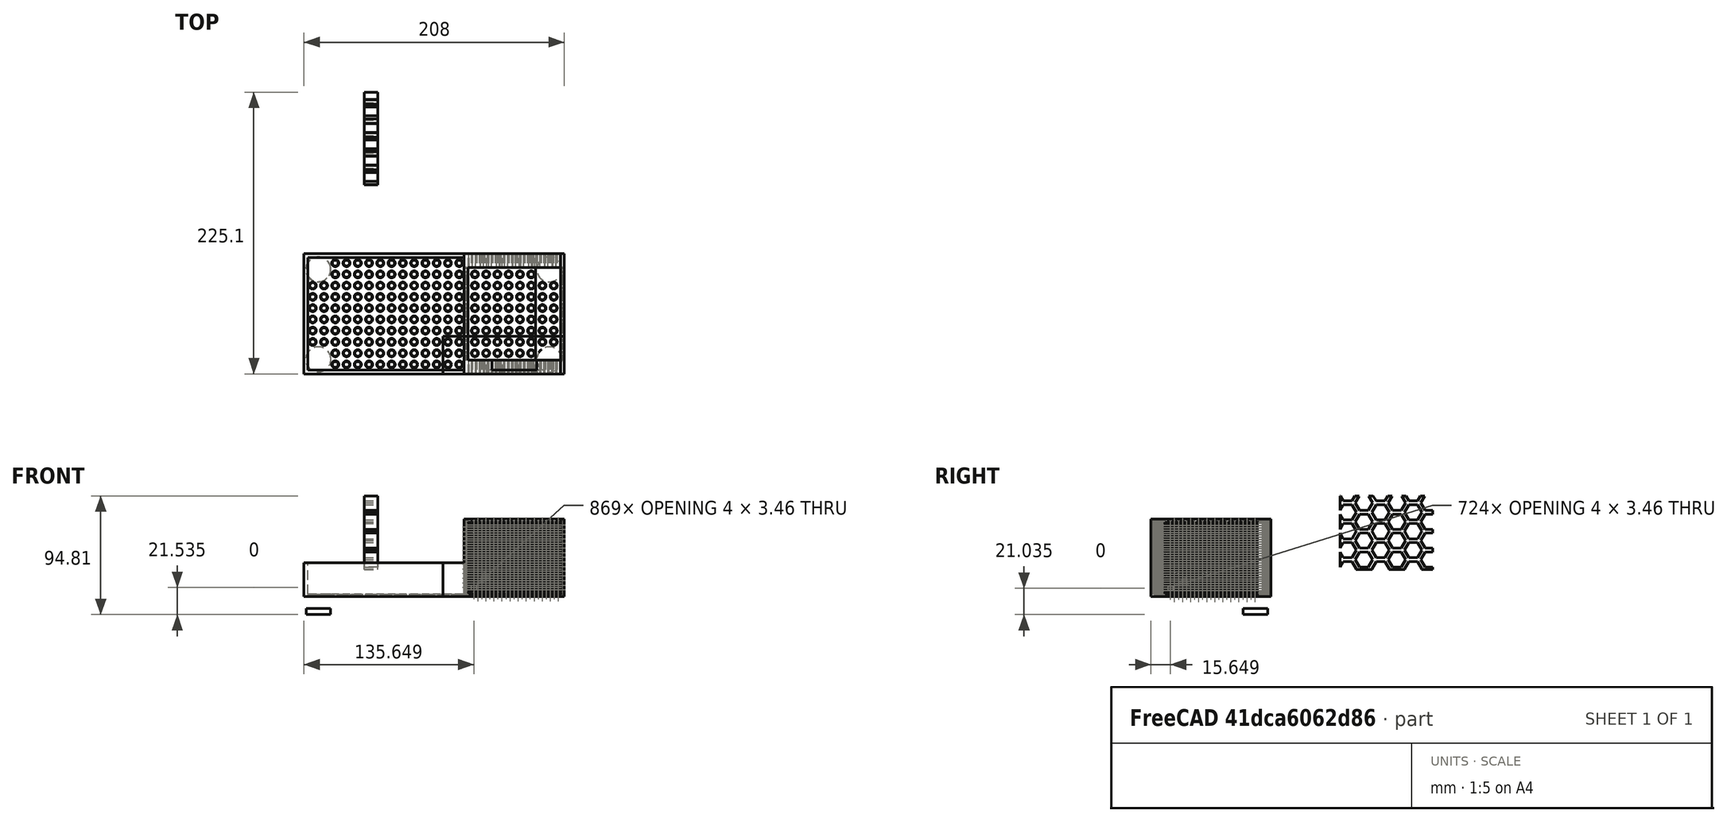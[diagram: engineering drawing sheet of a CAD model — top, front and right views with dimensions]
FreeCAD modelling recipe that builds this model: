
FCSTD DOCUMENT  (FreeCAD 0.19R24276 (Git))
Label: esponja_jabon19
License: All rights reserved
LicenseURL: http://en.wikipedia.org/wiki/All_rights_reserved
objects: Part::Box×18, Part::Cut×18, Part::Feature×10, Part::Cylinder×9, Part::MultiFuse×6, Part::FeaturePython×4, Mesh::Feature×3, Part::Cone×2, Spreadsheet::Sheet×1, Part::RegularPolygon×1, Part::Extrusion×1
note: 69 computed .brp shape members not serialized (recipe doc carries the construction recipe); baked Part::Feature solids carry a one-line shape summary decoded from their .brp

FEATURE [Part::Box] Box  label="Cube"
  AttacherType = Attacher::AttachEngine3D
  Height = 27
  Length = 128
  Width = 96
FEATURE [Part::Box] Box001  label="Cube001"
  AttacherType = Attacher::AttachEngine3D
  Height = 62
  Length = 125
  Placement = pos=(3,3,2) rot=(0,0,1;0rad)
  Width = 90
FEATURE [Part::Cut] Cut
  Base = -> Box
  Refine = true
  Tool = -> Box001
FEATURE [Part::Box] Box002  label="Cube002"
  AttacherType = Attacher::AttachEngine3D
  Height = 62
  Length = 80
  Placement = pos=(128,0,0) rot=(0,0,1;0rad)
  Width = 96
FEATURE [Part::Box] Box003  label="Cube003"
  AttacherType = Attacher::AttachEngine3D
  Height = 60
  Length = 74
  Placement = pos=(131,11,2) rot=(0,0,1;0rad)
  Width = 74
FEATURE [Part::Cone] Cone007  label="Cone001"
  Angle = 360
  AttacherType = Attacher::AttachEngine3D
  Height = 3
  Placement = pos=(7,7,0) rot=(0,0,1;0rad)
  Radius1 = 3
  Radius2 = 2.17
FEATURE [Part::Cone] Cone008
  Angle = 360
  AttacherType = Attacher::AttachEngine3D
  Height = 3
  Placement = pos=(135,16,0) rot=(0,0,1;0rad)
  Radius1 = 3
  Radius2 = 2.17
FEATURE [Part::Cylinder] Cylinder  label="Cylinder_up_left_add"
  Angle = 360
  AttacherType = Attacher::AttachEngine3D
  Height = 2
  Placement = pos=(11.5,11.5,0) rot=(0,0,1;0rad)
  Radius = 10
FEATURE [Part::Cylinder] Cylinder001  label="Cylinder001_down_left_add"
  Angle = 360
  AttacherType = Attacher::AttachEngine3D
  Height = 2
  Placement = pos=(11.5,83.5,0) rot=(0,0,1;0rad)
  Radius = 10
FEATURE [Part::Cylinder] Cylinder002  label="Cylinder002_up_right_Add"
  Angle = 360
  AttacherType = Attacher::AttachEngine3D
  Height = 2
  Placement = pos=(196,11.5,0) rot=(0,0,1;0rad)
  Radius = 10
FEATURE [Part::Cylinder] Cylinder003  label="Cylinder003_down_right_add"
  Angle = 360
  AttacherType = Attacher::AttachEngine3D
  Height = 2
  Placement = pos=(196,83.5,0) rot=(0,0,1;0rad)
  Radius = 10
FEATURE [Part::Cylinder] Cylinder004  label="Cylinder_up_left001_minus"
  Angle = 360
  AttacherType = Attacher::AttachEngine3D
  Height = 2
  Placement = pos=(11.5,11.5,-1.25) rot=(0,0,1;0rad)
  Radius = 10
FEATURE [Part::Cylinder] Cylinder005  label="Cylinder001_down_left001_minus"
  Angle = 360
  AttacherType = Attacher::AttachEngine3D
  Height = 2
  Placement = pos=(11.5,83.5,-1.25) rot=(0,0,1;0rad)
  Radius = 10
FEATURE [Part::Cylinder] Cylinder006  label="Cylinder002_up_right001_minus"
  Angle = 360
  AttacherType = Attacher::AttachEngine3D
  Height = 2
  Placement = pos=(196,11.5,-1.25) rot=(0,0,1;0rad)
  Radius = 10
FEATURE [Part::Cylinder] Cylinder007  label="Cylinder003_down_right001_minus"
  Angle = 360
  AttacherType = Attacher::AttachEngine3D
  Height = 2
  Placement = pos=(196,83.5,-1.25) rot=(0,0,1;0rad)
  Radius = 10
FEATURE [Spreadsheet::Sheet] EditMe
  cells = A1=User Variables; D1=Calculated Values; A2=Hexagon Radius:; B2(radius)=7; D2=X Interval:; E2(xInterval)==2 * sin(60deg) * (B2 * 2 + B3 - 0.267949 * B2); A3=Hexagon Separation:; B3(separation)=3; D3=Y Interval:; E3(yInterval)==2 * B2 + B3 - 0.267949 * B2; A4=Grid Width:; B4(width)=59; D4=First X:; E4(firstX)==B2; A5=Grid Length:; B5(length)=74; D5=First Y:; E5(firstY)==B2; A6=Grid Height:; B6(height)=11; D6=Count X:; E6(countX)==round(B5 / E2) + 2; D7=Count Y:; E7(countY)==round(B4 / E3) + 2; A8=Tweak X:; B8(tweakX)=0; D8=Array2 XPos:; E8(array2XPos)==sin(60deg) * (B2 * 2 + B3 - 0.267949 * B2); A9=Tweak Y:; B9(tweakY)=0; D9=Array2 YPos:; E9(array2YPos)==E3 / 2; A10=Tweak Z:; B10(tweakZ)=0; A11=Instructions:\n\nYou should only run the macro once unless you want to start again from scratch.\n\nEdit the values in column B to define your honeycomb.  You can also edit the objects (plate, arrays, etc.), but it's \nprobably better to do all the editing here in the spreadsheet at least until you get it more or less like you want it before\ndoing some final tweaking directly on the objects.\n\nHexagon radius -- the circumradius of the individual hexagons (circle with each vertex on its circumference).\n\nHexagon separation -- distance between each hexagon, the thickness of the grid produced after cutting the hexagons from the plate.\n\nPlate dimensions -- sets the dimensions of the plate out of which the honeycomb can be cut.  These values are used to calculate\nthe countX and countY variables.  You can delete the plate object if you wish to apply the hexagon arrays to a different structure.\n\nTweak X,Y,Z -- Edit these to move both hexagon arrays independently of the plate object, for example to center the arrays inside \nthe plate.\n\nCountX and CountY -- number of hexagons in the 2 arrays.  These are calculated based on the plate size, radius of hexagons, and \nseparation between them, but you will probably want to modify these manually.  Just remember if you modify them you are replacing \nthe formulas in those cells with immediate values, and thus they won't be recalulated for you if other changes are made.\n\nIf you would prefer a round plate, simply delete the plate object and replace it with a cylinder, and then use the Tweak values \nand countX and countY variables to arrange the hexagon arrays to your liking.
FEATURE [Part::RegularPolygon] HoneycombHexagon
  AttacherType = Attacher::AttachEngine3D
  Circumradius = 7
  Polygon = 6
  expr: Circumradius = EditMe.radius
FEATURE [Part::Extrusion] ExtrudedHexagon
  Base = -> HoneycombHexagon
  Dir = (0,0,1)
  DirMode = 0
  FaceMakerClass = Part::FaceMakerBullseye
  LengthFwd = 11
  LengthRev = 0
  Placement = pos=(7,7,0) rot=(0,0,1;0rad)
  Solid = true
  Symmetric = false
  expr: .Placement.Base.z = EditMe.tweakZ
  expr: .Placement.Base.y = EditMe.firstY + EditMe.tweakY
  expr: .Placement.Base.x = EditMe.firstX + EditMe.tweakX
  expr: LengthFwd = EditMe.height
FEATURE [Part::FeaturePython] HoneycombArray1  # Draft array (typed FeaturePython)
  Angle = 360
  ArrayType = 0
  Axis = (0,0,1)
  Base = -> ExtrudedHexagon
  Center = (0,0,0)
  Fuse = false
  IntervalAxis = (0,0,0)
  IntervalX = (26.1962,0,0)
  IntervalY = (0,15.1244,0)
  IntervalZ = (0,0,1)
  NumberPolar = 1
  NumberX = 5
  NumberY = 6
  NumberZ = 1
  expr: NumberY = EditMe.countY
  expr: NumberX = EditMe.countX
  expr: .IntervalY.y = EditMe.yInterval
  expr: .IntervalX.x = EditMe.xInterval
FEATURE [Part::FeaturePython] HoneycombArray2  # Draft array (typed FeaturePython)
  Angle = 360
  ArrayType = 0
  Axis = (0,0,1)
  Base = -> ExtrudedHexagon
  Center = (0,0,0)
  Fuse = false
  IntervalAxis = (0,0,0)
  IntervalX = (26.1962,0,0)
  IntervalY = (0,15.1244,0)
  IntervalZ = (0,0,1)
  NumberPolar = 1
  NumberX = 5
  NumberY = 6
  NumberZ = 1
  Placement = pos=(13.0981,7.56218,0) rot=(0,0,1;0rad)
  expr: NumberY = EditMe.countY
  expr: NumberX = EditMe.countX
  expr: .IntervalY.y = EditMe.yInterval
  expr: .IntervalX.x = EditMe.xInterval
  expr: .Placement.Base.y = EditMe.array2YPos
  expr: .Placement.Base.x = EditMe.array2XPos
FEATURE [Part::MultiFuse] Fused_Arrays
  Refine = true
  Shapes = -> [HoneycombArray1,HoneycombArray2]
FEATURE [Part::Box] Plate
  AttacherType = Attacher::AttachEngine3D
  Height = 11
  Length = 74
  Placement = pos=(27.0981,21.5622,0) rot=(0,0,1;0rad)
  Width = 59
  expr: .Placement.Base.y = EditMe.array2YPos + EditMe.radius * 2
  expr: .Placement.Base.x = EditMe.array2XPos + EditMe.radius * 2
  expr: Height = EditMe.height
  expr: Width = EditMe.width
  expr: Length = EditMe.length
FEATURE [Part::Cut] HoneycombGrid
  Base = -> Plate
  Placement = pos=(48,124,0) rot=(0.57735,0.57735,0.57735;2.0944rad)
  Refine = true
  Tool = -> Fused_Arrays
FEATURE [Part::Box] Box012  label="Cube012"
  AttacherType = Attacher::AttachEngine3D
  Height = 57
  Length = 73
  Placement = pos=(131.5,-0.5,2.5) rot=(0,0,1;0rad)
  Width = 12
FEATURE [Part::Box] Box014  label="Cube014"
  AttacherType = Attacher::AttachEngine3D
  Height = 57
  Length = 73
  Placement = pos=(209,11.5,2.5) rot=(0,0,1;1.5708rad)
  Width = 5
FEATURE [Part::Box] Box015  label="Cube015"
  AttacherType = Attacher::AttachEngine3D
  Height = 57
  Length = 73
  Placement = pos=(132,11.5,2.5) rot=(0,0,1;1.5708rad)
  Width = 5
FEATURE [Part::Cut] Cut001
  Base = -> Box002
  Refine = true
  Tool = -> Box003
FEATURE [Part::MultiFuse] Fusion
  Refine = true
  Shapes = -> [Cut,Cut001]
FEATURE [Part::Box] Box018  label="Cube018"
  AttacherType = Attacher::AttachEngine3D
  Height = 57
  Length = 73
  Placement = pos=(131.5,84.5,2.5) rot=(0,0,1;0rad)
  Width = 12
FEATURE [Part::Cut] Cut002
  Base = -> Fusion
  Refine = true
  Tool = -> Box018
FEATURE [Part::Cut] Cut003
  Base = -> Cut002
  Refine = true
  Tool = -> Box012
FEATURE [Part::Cut] Cut004
  Base = -> Cut003
  Refine = true
  Tool = -> Box014
FEATURE [Part::Cut] Cut005  label="pieza_sin_panel_sin_agujeros"
  Base = -> Cut004
  Refine = true
  Tool = -> Box015
FEATURE [Part::FeaturePython] Array  # Draft array (typed FeaturePython)
  Angle = 360
  ArrayType = 0
  Axis = (0,0,1)
  Base = -> Cone007
  Center = (0,0,0)
  Fuse = false
  IntervalAxis = (0,0,0)
  IntervalX = (9,0,0)
  IntervalY = (0,9,0)
  IntervalZ = (0,0,1)
  NumberPolar = 1
  NumberX = 14
  NumberY = 10
  NumberZ = 1
  Placement = pos=(0,95.5,2.5) rot=(1,0,0;3.14159rad)
FEATURE [Part::FeaturePython] Array001  # Draft array (typed FeaturePython)
  Angle = 360
  ArrayType = 0
  Axis = (0,0,1)
  Base = -> Cone008
  Center = (0,0,0)
  Fuse = false
  IntervalAxis = (0,0,0)
  IntervalX = (9,0,0)
  IntervalY = (0,9,0)
  IntervalZ = (0,0,1)
  NumberPolar = 1
  NumberX = 8
  NumberY = 8
  NumberZ = 1
  Placement = pos=(1.5,95.5,2.5) rot=(1,0,0;3.14159rad)
FEATURE [Part::Feature] HoneycombGrid001  label="HoneycombGrid_lateral1"
  Placement = pos=(124,11,-4) rot=(1,0,0;1.5708rad)
  shape: bbox 74 x 11 x 59 mm, 2299 faces (baked)
FEATURE [Part::Feature] HoneycombGrid003  label="HoneycombGrid_frente"
  Placement = pos=(205,4,-4.5) rot=(0.57735,0.57735,0.57735;2.0944rad)
  shape: bbox 3 x 74 x 59 mm, 2299 faces (baked)
FEATURE [Part::Feature] HoneycombGrid005  label="HoneycombGrid_lateral2"
  Placement = pos=(124,96,-4) rot=(1,0,0;1.5708rad)
  shape: bbox 74 x 11 x 59 mm, 2299 faces (baked)
FEATURE [Part::Feature] HoneycombGrid006  label="HoneycombGrid_fondo"
  Placement = pos=(128,4,-4.5) rot=(0.57735,0.57735,0.57735;2.0944rad)
  shape: bbox 3 x 74 x 59 mm, 2299 faces (baked)
FEATURE [Part::Cut] Cut006
  Base = -> Cut005
  Refine = true
  Tool = -> Array001
FEATURE [Part::Cut] Cut007  label="pieza_con_agujeros_base_sin_apoyos"
  Base = -> Cut006
  Refine = true
  Tool = -> Array
FEATURE [Part::Feature] Fusion002001  label="jabonera001"
  shape: bbox 208 x 96 x 62 mm, 9343 faces (baked)
FEATURE [Part::Box] Box019  label="Cube019"
  AttacherType = Attacher::AttachEngine3D
  Height = 70
  Length = 124
  Placement = pos=(-13,-9,0) rot=(0,0,1;0rad)
  Width = 124
FEATURE [Part::Cut] Cut012
  Base = -> Fusion002001
  Refine = true
  Tool = -> Box019
FEATURE [Part::Box] Box020  label="Cube020"
  AttacherType = Attacher::AttachEngine3D
  Height = 73
  Length = 100
  Placement = pos=(110,30,0) rot=(0,0,1;0rad)
  Width = 110
FEATURE [Part::Cut] Cut013
  Base = -> Cut012
  Refine = true
  Tool = -> Box020
FEATURE [Part::Box] Box021  label="Cube021"
  AttacherType = Attacher::AttachEngine3D
  Height = 60
  Length = 3
  Placement = pos=(205,27,0) rot=(0,0,1;0rad)
  Width = 3
FEATURE [Part::Box] Box022  label="Cube022"
  AttacherType = Attacher::AttachEngine3D
  Height = 60
  Length = 3
  Placement = pos=(128,27,0) rot=(0,0,1;0rad)
  Width = 3
FEATURE [Part::MultiFuse] Fusion002002  label="test_jabonera"
  Refine = true
  Shapes = -> [Cut013,Box022,Box021]
FEATURE [Part::Box] Box023  label="Cube023"
  AttacherType = Attacher::AttachEngine3D
  Height = 96
  Length = 36
  Placement = pos=(150,3,2) rot=(0,0,1;0rad)
  Width = 54
FEATURE [Part::Cut] Cut014
  Base = -> Fusion002002
  Refine = true
  Tool = -> Box023
FEATURE [Part::Box] Box024  label="Cube024"
  AttacherType = Attacher::AttachEngine3D
  Height = 60
  Length = 3
  Placement = pos=(147,3,2) rot=(0,0,1;0rad)
  Width = 8
FEATURE [Part::Box] Box025  label="Cube025"
  AttacherType = Attacher::AttachEngine3D
  Height = 60
  Length = 3
  Placement = pos=(186,3,2) rot=(0,0,1;0rad)
  Width = 8
FEATURE [Part::MultiFuse] Fusion002003  label="tes_jabonera_min"
  Refine = true
  Shapes = -> [Cut014,Box025,Box024]
FEATURE [Part::MultiFuse] Fusion002004  label="pieza_con_apoyos_rellenados"
  Shapes = -> [Cut007,Cylinder,Cylinder001,Cylinder002,Cylinder003]
FEATURE [Part::Cut] Cut015
  Base = -> Fusion002004
  Tool = -> Cylinder004
FEATURE [Part::Cut] Cut016
  Base = -> Cut015
  Tool = -> Cylinder007
FEATURE [Part::Cut] Cut017
  Base = -> Cut016
  Tool = -> Cylinder006
FEATURE [Part::Cut] Cut018  label="pieza_agujeros_no_panal_con_bases"
  Base = -> Cut017
  Tool = -> Cylinder005
FEATURE [Part::Feature] HoneycombGrid007  label="HoneycombGrid_fondo2"
  Placement = pos=(128,-16,-20) rot=(0.57735,0.57735,0.57735;2.0944rad)
  shape: bbox 3 x 74 x 59 mm, 157 faces (baked)
FEATURE [Part::Feature] HoneycombGrid007001  label="HoneycombGrid_frente2"
  Placement = pos=(205,-16,-20) rot=(0.57735,0.57735,0.57735;2.0944rad)
  shape: bbox 3 x 74 x 59 mm, 157 faces (baked)
FEATURE [Part::Feature] HoneycombGrid007002  label="HoneycombGrid_lateral2_1"
  Placement = pos=(104,11,-20) rot=(1,0,0;1.5708rad)
  shape: bbox 74 x 11 x 59 mm, 157 faces (baked)
FEATURE [Part::Feature] HoneycombGrid007003  label="HoneycombGrid_lateral2_002"
  Placement = pos=(104,96,-20) rot=(1,0,0;1.5708rad)
  shape: bbox 74 x 11 x 59 mm, 157 faces (baked)
FEATURE [Part::MultiFuse] Fusion002005  label="pieza_final_panal2"
  Shapes = -> [Cut018,HoneycombGrid007,HoneycombGrid007001,HoneycombGrid007002,HoneycombGrid007003]
FEATURE [Part::Feature] Fusion002005001  label="pieza_final_mini_2_completa"
  shape: bbox 208 x 96 x 62 mm, 987 faces (baked)
FEATURE [Part::Box] Box026  label="Cube026"
  AttacherType = Attacher::AttachEngine3D
  Height = 77
  Length = 205
  Placement = pos=(-20,-3,-3) rot=(0,0,1;0rad)
  Width = 110
FEATURE [Part::Cut] Cut019
  Base = -> Fusion002005001
  Tool = -> Box026
FEATURE [Part::Box] Box027  label="Cube027"
  AttacherType = Attacher::AttachEngine3D
  Height = 77
  Length = 205
  Placement = pos=(0,-3,2) rot=(0,0,1;0rad)
  Width = 110
FEATURE [Part::Cut] Cut020  label="test_mini_2"
  Base = -> Cut019
  Tool = -> Box027
FEATURE [Mesh::Feature] Mesh  label="test_mini_2 (Meshed)"
FEATURE [Part::Cylinder] Cylinder008  label="cilindro_pata"
  Angle = 360
  AttacherType = Attacher::AttachEngine3D
  Height = 5
  Placement = pos=(11.5,83.5,-14.25) rot=(0,0,1;0rad)
  Radius = 9.75
FEATURE [Mesh::Feature] Mesh001  label="cilindro_pata001"
FEATURE [Mesh::Feature] Mesh002  label="pieza_final_panal2 (Meshed)"
